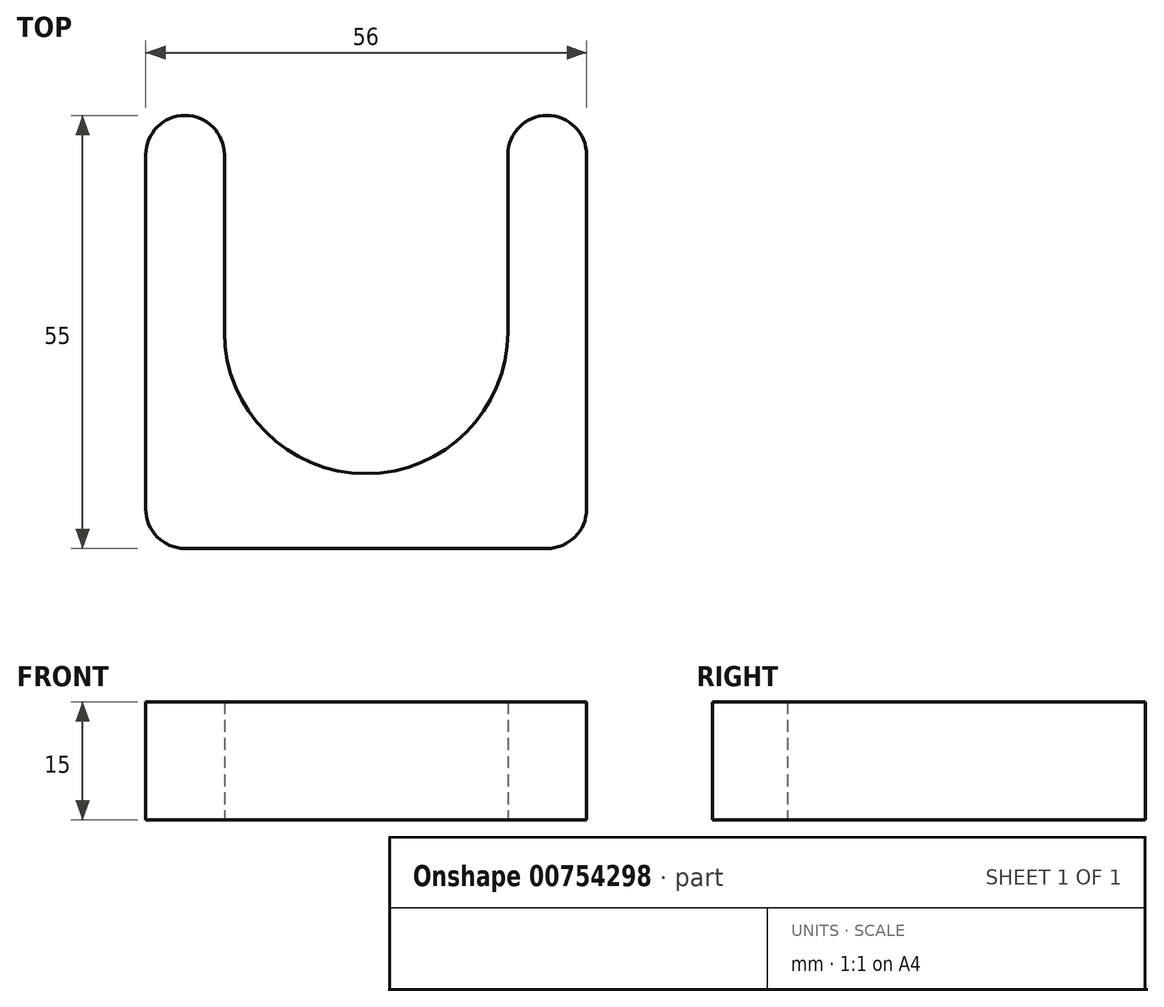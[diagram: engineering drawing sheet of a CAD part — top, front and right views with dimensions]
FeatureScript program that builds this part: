
annotation { "Feature Type Name" : "Feature", "Feature Type Description" : "" }
export const myFeature = defineFeature(function(context is Context, id is Id, definition is map)
    precondition{}
    {
        {
            var Q0;
            Q0=qCreatedBy(makeId("Top.planeOp"),FACE);
            var sketch = newSketch(context, id + "F0", { "sketchPlane" : qUnion([Q0])});
            skLineSegment(sketch, "E0.bottom", {"start": v(28, -27.5) * mm, "end": v(-28, -27.5) * mm});
            skLineSegment(sketch, "E0.top", {"start": v(28, 27.5) * mm, "end": v(18, 27.5) * mm});
            skLineSegment(sketch, "E0.left", {"start": v(28, -27.5) * mm, "end": v(28, 27.5) * mm});
            skLineSegment(sketch, "E0.right", {"start": v(-28, -27.5) * mm, "end": v(-28, 27.5) * mm});
            skPoint(sketch, "E0.middle", {"position": v(0, 0) * mm});
            skArc(sketch, "E1", {"start": v(-18, 0) * mm, "mid": v(0, -18) * mm, "end": v(18, 0) * mm});
            skLineSegment(sketch, "E2", {"start": v(-18, 0) * mm, "end": v(-18, 27.5) * mm});
            skLineSegment(sketch, "E3", {"start": v(18, 0) * mm, "end": v(18, 27.5) * mm});
            skLineSegment(sketch, "E4.trimOffspring", {"start": v(-18, 27.5) * mm, "end": v(-28, 27.5) * mm});
            skSolve(sketch);
        }
        {
            var Q0;
            Q0=makeQuery(id+"F0.imprint","IMPRINT",FACE,{"disambiguationData":[TD([[makeQuery(id+"F0.imprint","IMPRINT",EDGE,{"derivedFrom":sQuery(id+"F0.wireOp",EDGE,"E0.bottom")}),-1.0]])]});
            extrude(context, id + "F1", {"entities" : qUnion([Q0]), "depth" : 25 * mm, "offsetDistance" : 25 * mm});
        }
        {
            var Q0;
            Q0=makeQuery(id+"F1.opExtrude","SWEPT_EDGE",EDGE,{"disambiguationData":[OSD([sQuery(id+"F0.wireOp",EDGE,"E0.top"),sQuery(id+"F0.wireOp",EDGE,"E3")])]});
            var Q1;
            Q1=makeQuery(id+"F1.opExtrude","SWEPT_EDGE",EDGE,{"disambiguationData":[OSD([sQuery(id+"F0.wireOp",EDGE,"E2"),sQuery(id+"F0.wireOp",EDGE,"E4.trimOffspring")])]});
            var Q2;
            Q2=makeQuery(id+"F1.opExtrude","SWEPT_EDGE",EDGE,{"disambiguationData":[OSD([sQuery(id+"F0.wireOp",EDGE,"E0.top"),sQuery(id+"F0.wireOp",EDGE,"E0.left")])]});
            var Q3;
            Q3=makeQuery(id+"F1.opExtrude","SWEPT_EDGE",EDGE,{"disambiguationData":[OSD([sQuery(id+"F0.wireOp",EDGE,"E0.right"),sQuery(id+"F0.wireOp",EDGE,"E4.trimOffspring")])]});
            var Q4;
            Q4=makeQuery(id+"F1.opExtrude","SWEPT_EDGE",EDGE,{"disambiguationData":[OSD([sQuery(id+"F0.wireOp",EDGE,"E0.bottom"),sQuery(id+"F0.wireOp",EDGE,"E0.right")])]});
            var Q5;
            Q5=makeQuery(id+"F1.opExtrude","SWEPT_EDGE",EDGE,{"disambiguationData":[OSD([sQuery(id+"F0.wireOp",EDGE,"E0.bottom"),sQuery(id+"F0.wireOp",EDGE,"E0.left")])]});
            fillet(context, id + "F2", {"entities" : qUnion([Q0, Q1, Q2, Q3, Q4, Q5]), "radius" : 5 * mm, "tangentPropagation" : true, "allowEdgeOverflow" : false});
        }
        {
            var Q0;
            Q0=makeQuery(id+"F1.opExtrude","CAP_FACE",FACE,{"disambiguationData":[OSD([sQuery(id+"F0.wireOp",EDGE,"E0.bottom"),sQuery(id+"F0.wireOp",EDGE,"E0.top"),sQuery(id+"F0.wireOp",EDGE,"E0.left"),sQuery(id+"F0.wireOp",EDGE,"E0.right"),sQuery(id+"F0.wireOp",EDGE,"E1"),sQuery(id+"F0.wireOp",EDGE,"E2"),sQuery(id+"F0.wireOp",EDGE,"E3"),sQuery(id+"F0.wireOp",EDGE,"E4.trimOffspring")])],"isStart":false});
            extrude(context, id + "F3", {"entities" : qUnion([Q0]), "operationType" : NewBodyOperationType.ADD, "oppositeDirection" : true, "depth" : 15 * mm, "offsetDistance" : 25 * mm});
        }
        {
            var Q0;
            Q0=makeQuery(id+"F1.opExtrude","CAP_FACE",FACE,{"disambiguationData":[OSD([sQuery(id+"F0.wireOp",EDGE,"E0.bottom"),sQuery(id+"F0.wireOp",EDGE,"E0.top"),sQuery(id+"F0.wireOp",EDGE,"E0.left"),sQuery(id+"F0.wireOp",EDGE,"E0.right"),sQuery(id+"F0.wireOp",EDGE,"E1"),sQuery(id+"F0.wireOp",EDGE,"E2"),sQuery(id+"F0.wireOp",EDGE,"E3"),sQuery(id+"F0.wireOp",EDGE,"E4.trimOffspring")])],"isStart":false});
            extrude(context, id + "F4", {"entities" : qUnion([Q0]), "operationType" : NewBodyOperationType.REMOVE, "oppositeDirection" : true, "depth" : 10 * mm, "offsetDistance" : 25 * mm});
        }
    });
